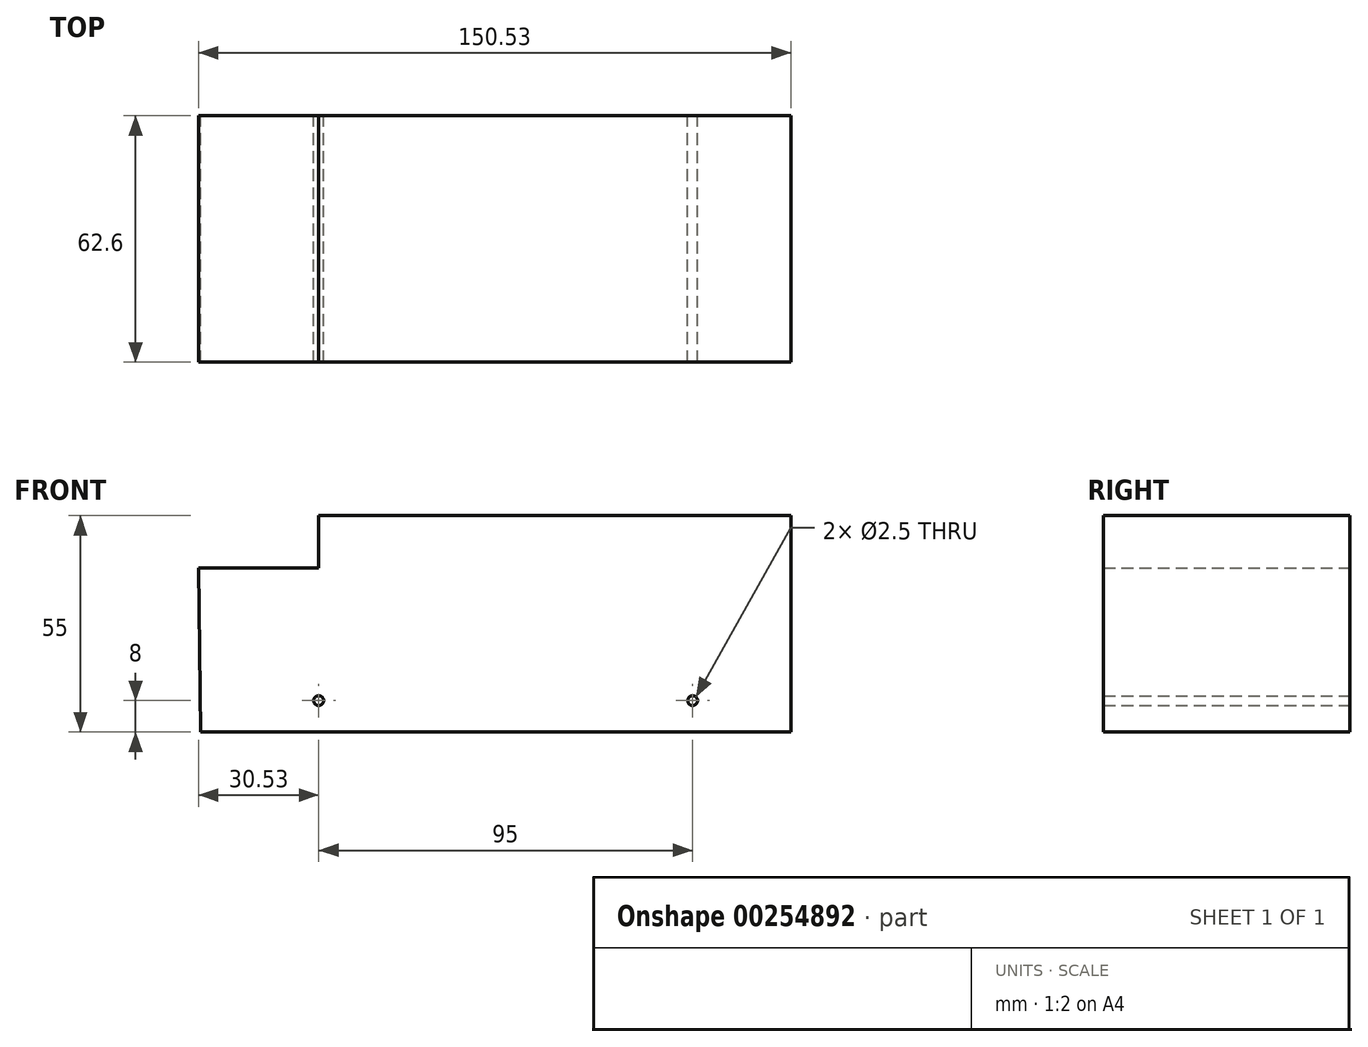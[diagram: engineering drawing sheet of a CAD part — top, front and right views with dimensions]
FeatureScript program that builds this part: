
annotation { "Feature Type Name" : "Feature", "Feature Type Description" : "" }
export const myFeature = defineFeature(function(context is Context, id is Id, definition is map)
    precondition{}
    {
        {
            var Q0;
            Q0=qCreatedBy(makeId("Front.planeOp"),FACE);
            var sketch = newSketch(context, id + "F0", { "sketchPlane" : qUnion([Q0])});
            skLineSegment(sketch, "E0.bottom", {"start": v(60, 27.5) * mm, "end": v(-60, 27.5) * mm});
            skLineSegment(sketch, "E0.top", {"start": v(60, -27.5) * mm, "end": v(-60, -27.5) * mm});
            skLineSegment(sketch, "E0.left", {"start": v(60, 27.5) * mm, "end": v(60, -27.5) * mm});
            skPoint(sketch, "E0.middle", {"position": v(0, 0) * mm});
            skLineSegment(sketch, "E1", {"start": v(-60, -27.5) * mm, "end": v(-90, -27.5) * mm});
            skLineSegment(sketch, "E2", {"start": v(60, -27.5) * mm, "end": v(35, -27.5) * mm});
            skLineSegment(sketch, "E3", {"start": v(-60, 27.5) * mm, "end": v(-60, 14.2) * mm});
            skLineSegment(sketch, "E4", {"start": v(-60, 14.2) * mm, "end": v(-90.53, 14.2) * mm});
            skLineSegment(sketch, "E5", {"start": v(-90.53, 14.2) * mm, "end": v(-90, -27.5) * mm});
            skLineSegment(sketch, "E6", {"start": v(35, -27.5) * mm, "end": v(35, -19.5) * mm});
            skLineSegment(sketch, "E7", {"start": v(-60, -27.5) * mm, "end": v(-60, -19.5) * mm});
            skCircle(sketch, "E8", {"center": v(-60, -19.5) * mm, "radius": 1.25 * mm});
            skCircle(sketch, "E9", {"center": v(35, -19.5) * mm, "radius": 1.25 * mm});
            skSolve(sketch);
        }
        {
            var Q0;
            Q0 = qSketchRegion(id + "F0", true);
            extrude(context, id + "F1", {"entities" : qUnion([Q0]), "depth" : 25 * mm});
        }
        {
            var Q0;
            Q0 = qSketchRegion(id + "F0", true);
            extrude(context, id + "F2", {"entities" : qUnion([Q0]), "operationType" : NewBodyOperationType.ADD, "depth" : 37.6 * mm});
        }
        {
            var Q0;
            Q0=makeQuery(id+"F0.imprint","IMPRINT",FACE,{"disambiguationData":[TD([[makeQuery(id+"F0.imprint","IMPRINT",EDGE,{"derivedFrom":sQuery(id+"F0.wireOp",EDGE,"E0.bottom")}),1.0]])]});
            extrude(context, id + "F3", {"entities" : qUnion([Q0]), "operationType" : NewBodyOperationType.ADD, "depth" : 25 * mm});
        }
        {
            var Q0;
            Q0=makeQuery(id+"F2.opExtrude","CAP_FACE",FACE,{"disambiguationData":[OSD([sQuery(id+"F0.wireOp",EDGE,"E0.bottom"),sQuery(id+"F0.wireOp",EDGE,"E0.top"),sQuery(id+"F0.wireOp",EDGE,"E0.left"),sQuery(id+"F0.wireOp",EDGE,"E1"),sQuery(id+"F0.wireOp",EDGE,"E2"),sQuery(id+"F0.wireOp",EDGE,"E3"),sQuery(id+"F0.wireOp",EDGE,"E4"),sQuery(id+"F0.wireOp",EDGE,"E5"),sQuery(id+"F0.wireOp",EDGE,"E8"),sQuery(id+"F0.wireOp",EDGE,"E9"),sQuery(id+"F0.wireOp",EDGE,"hj32Iiem-WZ0a-ZO8Y-bq9b-d4wMV3hambWd"),sQuery(id+"F0.wireOp",EDGE,"fT2fXTMt-VHBQ-83md-7mJc-ZcUuqmqaZhXG")])],"isStart":false});
            extrude(context, id + "F4", {"entities" : qUnion([Q0]), "operationType" : NewBodyOperationType.ADD, "depth" : 25 * mm});
        }
        {
            var Q0;
            Q0=makeQuery(id+"F0.imprint","IMPRINT",FACE,{"disambiguationData":[TD([[makeQuery(id+"F0.imprint","IMPRINT",EDGE,{"derivedFrom":sQuery(id+"F0.wireOp",EDGE,"E0.bottom")}),1.0]])]});
            extrude(context, id + "F5", {"entities" : qUnion([Q0]), "operationType" : NewBodyOperationType.ADD, "depth" : 25 * mm});
        }
    });
